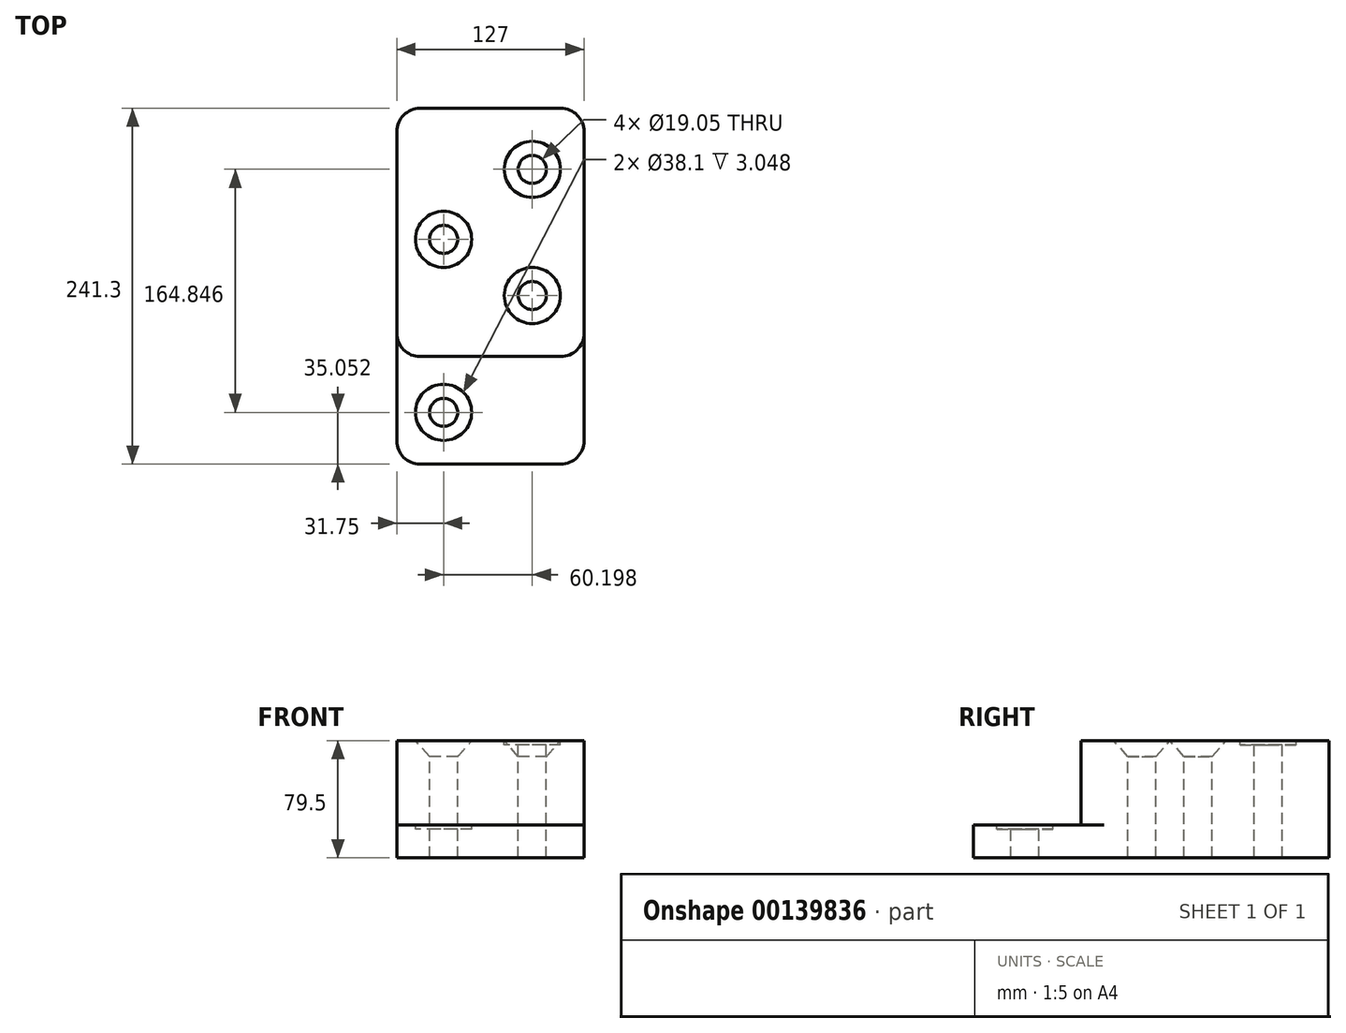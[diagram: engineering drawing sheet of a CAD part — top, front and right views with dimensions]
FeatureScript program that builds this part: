
annotation { "Feature Type Name" : "Feature", "Feature Type Description" : "" }
export const myFeature = defineFeature(function(context is Context, id is Id, definition is map)
    precondition{}
    {
        {
            var Q0;
            Q0=qCreatedBy(makeId("Top.planeOp"),FACE);
            var sketch = newSketch(context, id + "F0", { "sketchPlane" : qUnion([Q0])});
            skLineSegment(sketch, "E0.bottom", {"start": v(15.75, 0) * mm, "end": v(111.25, 0) * mm});
            skLineSegment(sketch, "E0.top", {"start": v(15.75, 241.3) * mm, "end": v(111.25, 241.3) * mm});
            skLineSegment(sketch, "E0.left", {"start": v(0, 88.65) * mm, "end": v(0, 225.55) * mm});
            skLineSegment(sketch, "E0.right", {"start": v(127, 88.65) * mm, "end": v(127, 225.55) * mm});
            skLineSegment(sketch, "E1", {"start": v(15.75, 72.9) * mm, "end": v(111.25, 72.9) * mm});
            skPoint(sketch, "E2.visualSharp", {"position": v(127, 0) * mm});
            skArc(sketch, "E2.filletArc", {"start": v(111.25, 0) * mm, "mid": v(122.39, 4.61) * mm, "end": v(127, 15.75) * mm});
            skPoint(sketch, "E3.visualSharp", {"position": v(0, 0) * mm});
            skArc(sketch, "E3.filletArc", {"start": v(0, 15.75) * mm, "mid": v(4.61, 4.61) * mm, "end": v(15.75, 0) * mm});
            skArc(sketch, "E4.filletArc", {"start": v(111.25, 72.9) * mm, "mid": v(122.39, 77.51) * mm, "end": v(127, 88.65) * mm});
            skArc(sketch, "E5.filletArc", {"start": v(0, 88.65) * mm, "mid": v(4.61, 77.51) * mm, "end": v(15.75, 72.9) * mm});
            skPoint(sketch, "E6.visualSharp", {"position": v(127, 241.3) * mm});
            skArc(sketch, "E6.filletArc", {"start": v(127, 225.55) * mm, "mid": v(122.39, 236.69) * mm, "end": v(111.25, 241.3) * mm});
            skPoint(sketch, "E7.visualSharp", {"position": v(0, 241.3) * mm});
            skArc(sketch, "E7.filletArc", {"start": v(15.75, 241.3) * mm, "mid": v(4.61, 236.69) * mm, "end": v(0, 225.55) * mm});
            skLineSegment(sketch, "E8", {"start": v(0, 15.75) * mm, "end": v(0, 88.65) * mm});
            skLineSegment(sketch, "E9", {"start": v(127, 15.75) * mm, "end": v(127, 88.65) * mm});
            skPoint(sketch, "E10", {"position": v(31.75, 35.05) * mm});
            skPoint(sketch, "E11", {"position": v(91.95, 114.3) * mm});
            skPoint(sketch, "E12", {"position": v(31.75, 152.4) * mm});
            skPoint(sketch, "E13", {"position": v(91.95, 199.9) * mm});
            skSolve(sketch);
        }
        {
            var Q0;
            Q0=makeQuery(id+"F0.imprint","IMPRINT",FACE,{"disambiguationData":[TD([[makeQuery(id+"F0.imprint","IMPRINT",EDGE,{"derivedFrom":sQuery(id+"F0.wireOp",EDGE,"E0.bottom")}),1.0]])]});
            extrude(context, id + "F1", {"entities" : qUnion([Q0]), "depth" : 22.35 * mm});
        }
        {
            var Q0;
            Q0=makeQuery(id+"F0.imprint","IMPRINT",FACE,{"disambiguationData":[TD([[makeQuery(id+"F0.imprint","IMPRINT",EDGE,{"derivedFrom":sQuery(id+"F0.wireOp",EDGE,"E0.top")}),-1.0]])]});
            extrude(context, id + "F2", {"entities" : qUnion([Q0]), "operationType" : NewBodyOperationType.ADD, "depth" : 79.5 * mm});
        }
        {
            var Q0;
            Q0=makeQuery(id+"F2.opExtrude","CAP_FACE",FACE,{"disambiguationData":[OSD([sQuery(id+"F0.wireOp",EDGE,"E0.top"),sQuery(id+"F0.wireOp",EDGE,"E0.left"),sQuery(id+"F0.wireOp",EDGE,"E0.right"),sQuery(id+"F0.wireOp",EDGE,"E1"),sQuery(id+"F0.wireOp",EDGE,"E4.filletArc"),sQuery(id+"F0.wireOp",EDGE,"E5.filletArc"),sQuery(id+"F0.wireOp",EDGE,"E6.filletArc"),sQuery(id+"F0.wireOp",EDGE,"E7.filletArc")])],"isStart":false});
            var sketch = newSketch(context, id + "F3", { "sketchPlane" : qUnion([Q0])});
            skPoint(sketch, "E14.0", {"position": v(91.95, 114.3) * mm});
            skPoint(sketch, "E15.0", {"position": v(31.75, 152.4) * mm});
            skPoint(sketch, "E16.0", {"position": v(91.95, 199.9) * mm});
            skSolve(sketch);
        }
        {
            var Q0;
            Q0=sQuery(id+"F3.wireOp",VERTEX,"E16.0");
            var Q1;
            Q1=makeQuery(id+"F1.opExtrude","SWEPT_BODY",BODY,{"disambiguationData":[OSD([sQuery(id+"F0.wireOp",EDGE,"E0.bottom"),sQuery(id+"F0.wireOp",EDGE,"E1"),sQuery(id+"F0.wireOp",EDGE,"E2.filletArc"),sQuery(id+"F0.wireOp",EDGE,"E3.filletArc"),sQuery(id+"F0.wireOp",EDGE,"E4.filletArc"),sQuery(id+"F0.wireOp",EDGE,"E5.filletArc"),sQuery(id+"F0.wireOp",EDGE,"E8"),sQuery(id+"F0.wireOp",EDGE,"E9")])]});
            hole(context, id + "F4", {"style" : HoleStyle.C_BORE, "endStyle" : HoleEndStyle.THROUGH, "holeDiameter" : 19.05 * mm, "cBoreDiameter" : 38.1 * mm, "cBoreDepth" : 3.05 * mm, "locations" : qUnion([Q0]), "scope" : qUnion([Q1]), "isTappedThrough" : true});
        }
        {
            var Q0;
            Q0=sQuery(id+"F3.wireOp",VERTEX,"E15.0");
            var Q1;
            Q1=makeQuery(id+"F1.opExtrude","SWEPT_BODY",BODY,{"disambiguationData":[OSD([sQuery(id+"F0.wireOp",EDGE,"E0.bottom"),sQuery(id+"F0.wireOp",EDGE,"E1"),sQuery(id+"F0.wireOp",EDGE,"E2.filletArc"),sQuery(id+"F0.wireOp",EDGE,"E3.filletArc"),sQuery(id+"F0.wireOp",EDGE,"E4.filletArc"),sQuery(id+"F0.wireOp",EDGE,"E5.filletArc"),sQuery(id+"F0.wireOp",EDGE,"E8"),sQuery(id+"F0.wireOp",EDGE,"E9")])]});
            hole(context, id + "F5", {"style" : HoleStyle.C_SINK, "endStyle" : HoleEndStyle.THROUGH, "holeDiameter" : 19.05 * mm, "cSinkDiameter" : 38.1 * mm, "cSinkAngle" : 82 * degree, "locations" : qUnion([Q0]), "scope" : qUnion([Q1]), "isTappedThrough" : true});
        }
        {
            var Q0;
            Q0=sQuery(id+"F3.wireOp",VERTEX,"E14.0");
            var Q1;
            Q1=makeQuery(id+"F1.opExtrude","SWEPT_BODY",BODY,{"disambiguationData":[OSD([sQuery(id+"F0.wireOp",EDGE,"E0.bottom"),sQuery(id+"F0.wireOp",EDGE,"E1"),sQuery(id+"F0.wireOp",EDGE,"E2.filletArc"),sQuery(id+"F0.wireOp",EDGE,"E3.filletArc"),sQuery(id+"F0.wireOp",EDGE,"E4.filletArc"),sQuery(id+"F0.wireOp",EDGE,"E5.filletArc"),sQuery(id+"F0.wireOp",EDGE,"E8"),sQuery(id+"F0.wireOp",EDGE,"E9")])]});
            hole(context, id + "F6", {"style" : HoleStyle.C_SINK, "endStyle" : HoleEndStyle.THROUGH, "holeDiameter" : 19.05 * mm, "cSinkDiameter" : 38.1 * mm, "cSinkAngle" : 82 * degree, "locations" : qUnion([Q0]), "scope" : qUnion([Q1]), "isTappedThrough" : true});
        }
        {
            var Q0;
            Q0=makeQuery(id+"F1.opExtrude","CAP_FACE",FACE,{"disambiguationData":[OSD([sQuery(id+"F0.wireOp",EDGE,"E0.bottom"),sQuery(id+"F0.wireOp",EDGE,"E1"),sQuery(id+"F0.wireOp",EDGE,"E2.filletArc"),sQuery(id+"F0.wireOp",EDGE,"E3.filletArc"),sQuery(id+"F0.wireOp",EDGE,"E4.filletArc"),sQuery(id+"F0.wireOp",EDGE,"E5.filletArc"),sQuery(id+"F0.wireOp",EDGE,"E8"),sQuery(id+"F0.wireOp",EDGE,"E9")])],"isStart":false});
            var sketch = newSketch(context, id + "F7", { "sketchPlane" : qUnion([Q0])});
            skPoint(sketch, "E17.0", {"position": v(31.75, 35.05) * mm});
            skSolve(sketch);
        }
        {
            var Q0;
            Q0=sQuery(id+"F7.wireOp",VERTEX,"E17.0");
            var Q1;
            Q1=makeQuery(id+"F1.opExtrude","SWEPT_BODY",BODY,{"disambiguationData":[OSD([sQuery(id+"F0.wireOp",EDGE,"E0.bottom"),sQuery(id+"F0.wireOp",EDGE,"E1"),sQuery(id+"F0.wireOp",EDGE,"E2.filletArc"),sQuery(id+"F0.wireOp",EDGE,"E3.filletArc"),sQuery(id+"F0.wireOp",EDGE,"E4.filletArc"),sQuery(id+"F0.wireOp",EDGE,"E5.filletArc"),sQuery(id+"F0.wireOp",EDGE,"E8"),sQuery(id+"F0.wireOp",EDGE,"E9")])]});
            hole(context, id + "F8", {"style" : HoleStyle.C_BORE, "endStyle" : HoleEndStyle.THROUGH, "holeDiameter" : 19.05 * mm, "cBoreDiameter" : 38.1 * mm, "cBoreDepth" : 3.05 * mm, "locations" : qUnion([Q0]), "scope" : qUnion([Q1]), "isTappedThrough" : true});
        }
    });
